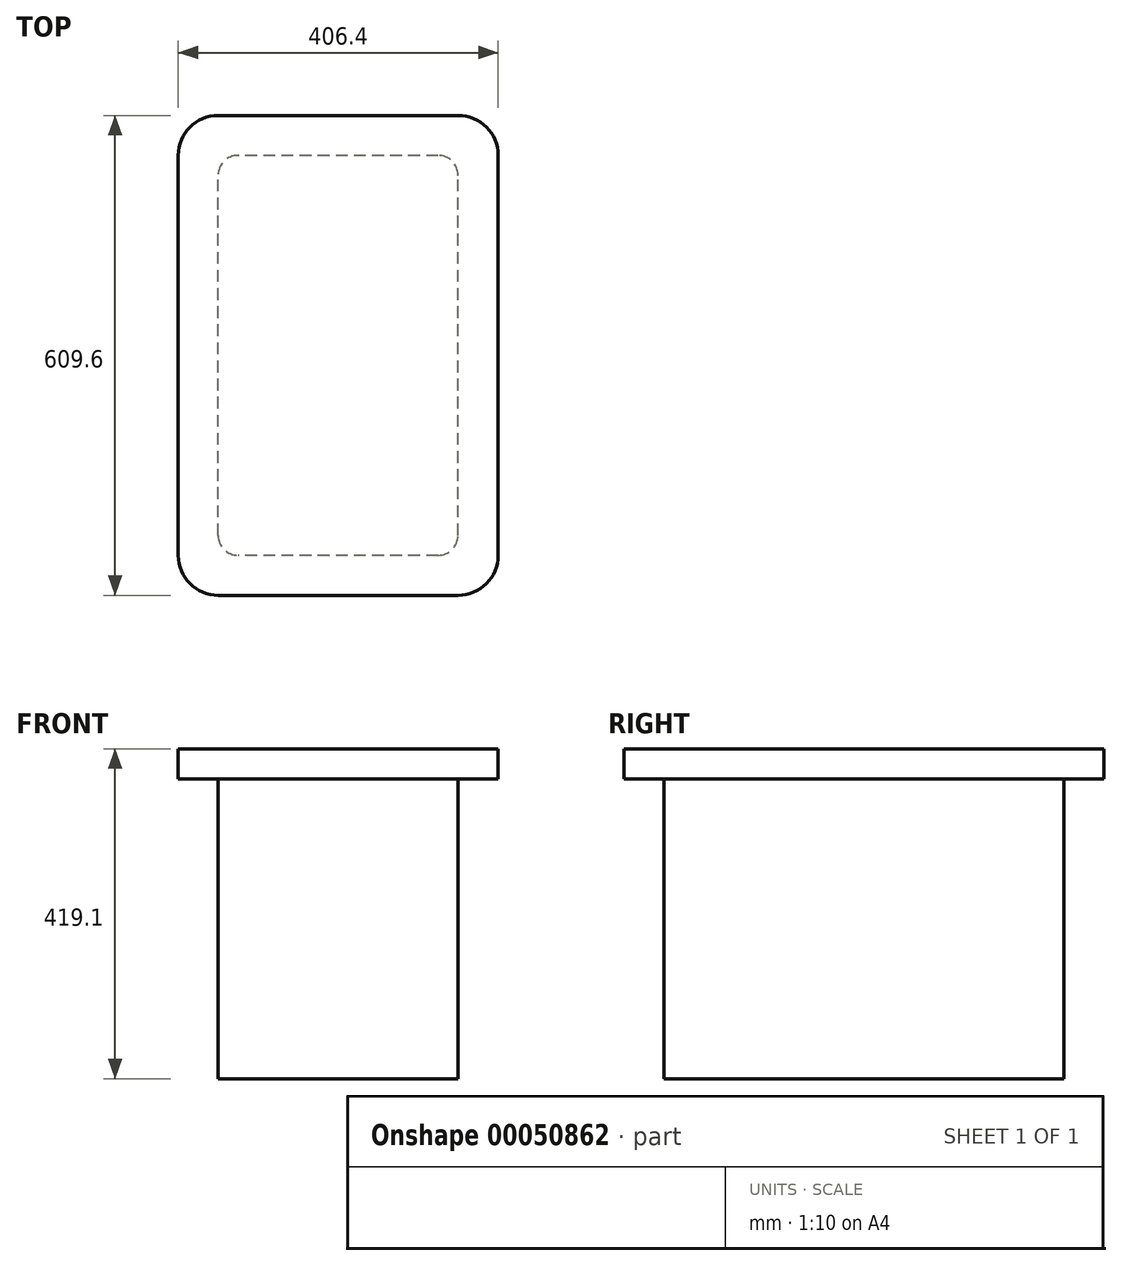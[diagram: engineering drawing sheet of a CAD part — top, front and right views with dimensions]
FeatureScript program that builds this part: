
annotation { "Feature Type Name" : "Feature", "Feature Type Description" : "" }
export const myFeature = defineFeature(function(context is Context, id is Id, definition is map)
    precondition{}
    {
        {
            var Q0;
            Q0=qCreatedBy(makeId("Top.planeOp"),FACE);
            var sketch = newSketch(context, id + "F0", { "sketchPlane" : qUnion([Q0])});
            skLineSegment(sketch, "E0.rect.bottom", {"start": v(203.2, 304.8) * mm, "end": v(-203.2, 304.8) * mm});
            skLineSegment(sketch, "E0.rect.top", {"start": v(203.2, -304.8) * mm, "end": v(-203.2, -304.8) * mm});
            skLineSegment(sketch, "E0.rect.left", {"start": v(203.2, 304.8) * mm, "end": v(203.2, -304.8) * mm});
            skLineSegment(sketch, "E0.rect.right", {"start": v(-203.2, 304.8) * mm, "end": v(-203.2, -304.8) * mm});
            skPoint(sketch, "E0.rect.middle", {"position": v(0, 0) * mm});
            skSolve(sketch);
        }
        {
            var Q0;
            Q0=qSketchRegion(id+"F0",true);
            extrude(context, id + "F1", {"entities" : qUnion([Q0]), "depth" : 419.1 * mm});
        }
        {
            var Q0;
            Q0=makeQuery(id+"F1.opExtrude","SWEPT_EDGE",EDGE,{"disambiguationData":[OSD([sQuery(id+"F0.wireOp",EDGE,"E0.rect.bottom"),sQuery(id+"F0.wireOp",EDGE,"E0.rect.right")])]});
            var Q1;
            Q1=makeQuery(id+"F1.opExtrude","SWEPT_EDGE",EDGE,{"disambiguationData":[OSD([sQuery(id+"F0.wireOp",EDGE,"E0.rect.bottom"),sQuery(id+"F0.wireOp",EDGE,"E0.rect.left")])]});
            var Q2;
            Q2=makeQuery(id+"F1.opExtrude","SWEPT_EDGE",EDGE,{"disambiguationData":[OSD([sQuery(id+"F0.wireOp",EDGE,"E0.rect.top"),sQuery(id+"F0.wireOp",EDGE,"E0.rect.right")])]});
            var Q3;
            Q3=makeQuery(id+"F1.opExtrude","SWEPT_EDGE",EDGE,{"disambiguationData":[OSD([sQuery(id+"F0.wireOp",EDGE,"E0.rect.top"),sQuery(id+"F0.wireOp",EDGE,"E0.rect.left")])]});
            fillet(context, id + "F2", {"entities" : qUnion([Q0, Q1, Q2, Q3]), "radius" : 50.8 * mm, "tangentPropagation" : true, "allowEdgeOverflow" : false});
        }
        {
            var Q0;
            Q0=makeQuery(id+"F1.opExtrude","CAP_FACE",FACE,{"disambiguationData":[OSD([sQuery(id+"F0.wireOp",EDGE,"E0.rect.bottom"),sQuery(id+"F0.wireOp",EDGE,"E0.rect.top"),sQuery(id+"F0.wireOp",EDGE,"E0.rect.left"),sQuery(id+"F0.wireOp",EDGE,"E0.rect.right")])],"isStart":true});
            var sketch = newSketch(context, id + "F3", { "sketchPlane" : qUnion([Q0])});
            skLineSegment(sketch, "E1.rect.bottom", {"start": v(127, 254) * mm, "end": v(-127, 254) * mm});
            skLineSegment(sketch, "E1.rect.top", {"start": v(127, -254) * mm, "end": v(-127, -254) * mm});
            skLineSegment(sketch, "E1.rect.left", {"start": v(152.4, 228.6) * mm, "end": v(152.4, -228.6) * mm});
            skLineSegment(sketch, "E1.rect.right", {"start": v(-152.4, 228.6) * mm, "end": v(-152.4, -228.6) * mm});
            skPoint(sketch, "E1.rect.middle", {"position": v(0, 0) * mm});
            skPoint(sketch, "E2.visualSharp", {"position": v(-152.4, 254) * mm});
            skArc(sketch, "E2.filletArc", {"start": v(-127, 254) * mm, "mid": v(-144.96, 246.56) * mm, "end": v(-152.4, 228.6) * mm});
            skPoint(sketch, "E3.visualSharp", {"position": v(152.4, 254) * mm});
            skArc(sketch, "E3.filletArc", {"start": v(152.4, 228.6) * mm, "mid": v(144.96, 246.56) * mm, "end": v(127, 254) * mm});
            skPoint(sketch, "E4.visualSharp", {"position": v(152.4, -254) * mm});
            skArc(sketch, "E4.filletArc", {"start": v(127, -254) * mm, "mid": v(144.96, -246.56) * mm, "end": v(152.4, -228.6) * mm});
            skPoint(sketch, "E5.visualSharp", {"position": v(-152.4, -254) * mm});
            skArc(sketch, "E5.filletArc", {"start": v(-152.4, -228.6) * mm, "mid": v(-144.96, -246.56) * mm, "end": v(-127, -254) * mm});
            skSolve(sketch);
        }
        {
            var Q0;
            Q0=makeQuery(id+"F3.imprint","IMPRINT",FACE,{"disambiguationData":[TD([[makeQuery(id+"F3.imprint","IMPRINT",EDGE,{"derivedFrom":sQuery(id+"F3.wireOp",EDGE,"E1.rect.bottom")}),-1.0]])]});
            extrude(context, id + "F4", {"entities" : qUnion([Q0]), "operationType" : NewBodyOperationType.REMOVE, "oppositeDirection" : true, "depth" : 381 * mm});
        }
    });
